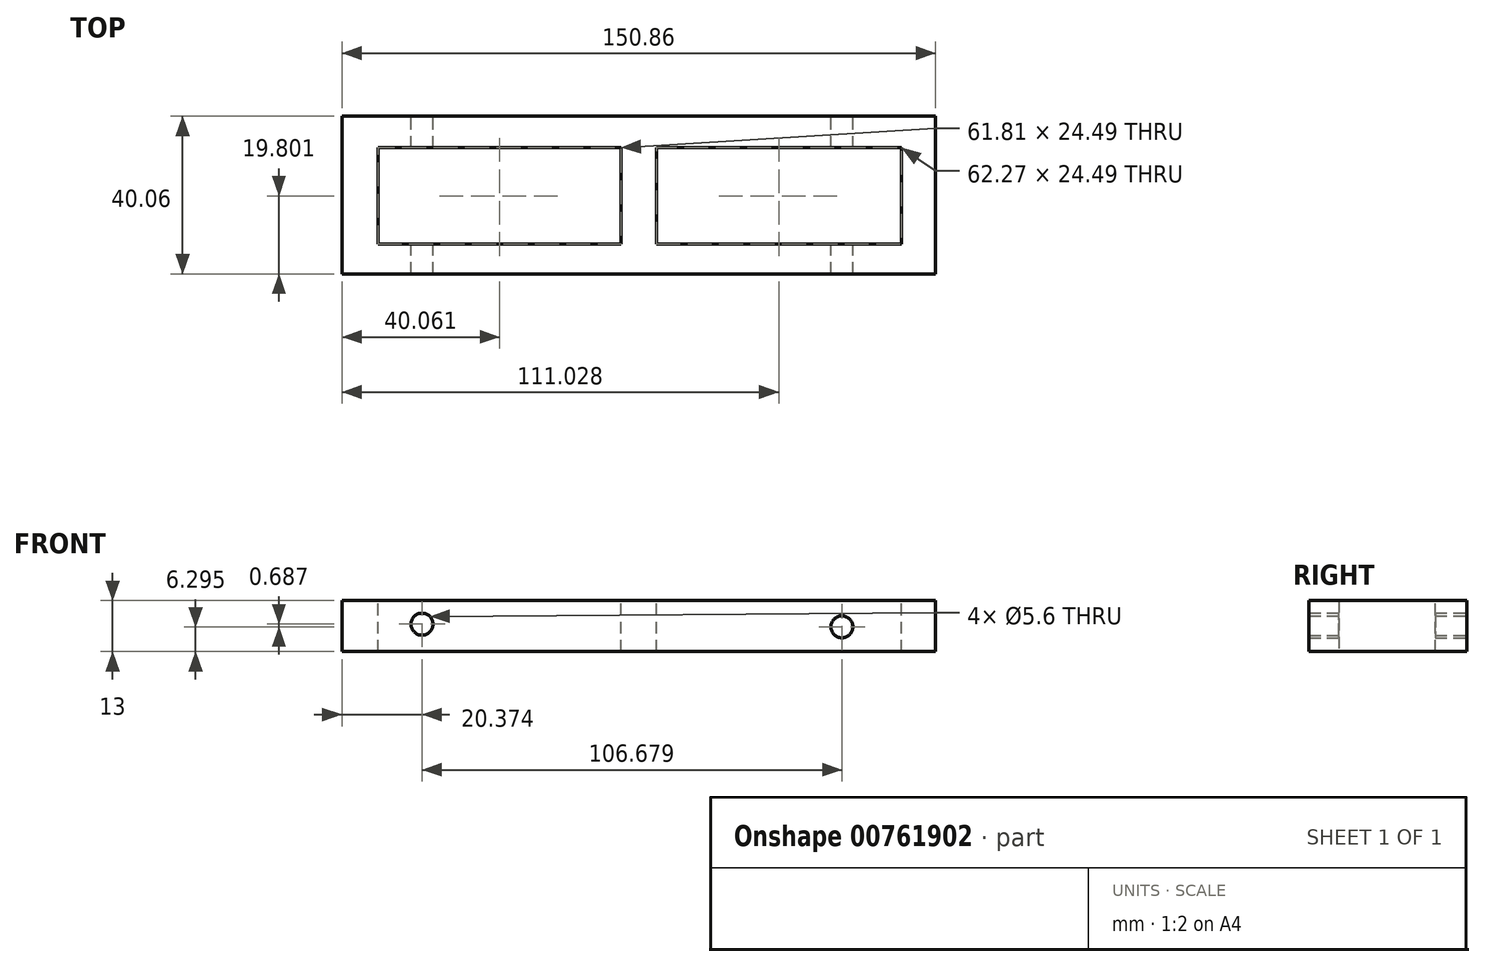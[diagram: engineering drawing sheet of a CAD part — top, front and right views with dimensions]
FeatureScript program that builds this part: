
annotation { "Feature Type Name" : "Feature", "Feature Type Description" : "" }
export const myFeature = defineFeature(function(context is Context, id is Id, definition is map)
    precondition{}
    {
        {
            var Q0;
            Q0=qCreatedBy(makeId("Top.planeOp"),FACE);
            var sketch = newSketch(context, id + "F0", { "sketchPlane" : qUnion([Q0])});
            skLineSegment(sketch, "E0.bottom", {"start": v(75.43, 20.03) * mm, "end": v(-75.43, 20.03) * mm});
            skLineSegment(sketch, "E0.top", {"start": v(75.43, -20.03) * mm, "end": v(-75.43, -20.03) * mm});
            skLineSegment(sketch, "E0.left", {"start": v(75.43, 20.03) * mm, "end": v(75.43, -20.03) * mm});
            skLineSegment(sketch, "E0.right", {"start": v(-75.43, 20.03) * mm, "end": v(-75.43, -20.03) * mm});
            skPoint(sketch, "E0.middle", {"position": v(0, 0) * mm});
            skSolve(sketch);
        }
        {
            var Q0;
            Q0=makeQuery(id+"F0.imprint","IMPRINT",FACE,{"disambiguationData":[TD([[makeQuery(id+"F0.imprint","IMPRINT",EDGE,{"derivedFrom":sQuery(id+"F0.wireOp",EDGE,"E0.bottom")}),1.0]])]});
            extrude(context, id + "F1", {"entities" : qUnion([Q0]), "depth" : 13 * mm, "offsetDistance" : 25 * mm});
        }
        {
            var Q0;
            Q0=makeQuery(id+"F1.opExtrude","CAP_FACE",FACE,{"disambiguationData":[OSD([sQuery(id+"F0.wireOp",EDGE,"E0.bottom"),sQuery(id+"F0.wireOp",EDGE,"E0.top"),sQuery(id+"F0.wireOp",EDGE,"E0.left"),sQuery(id+"F0.wireOp",EDGE,"E0.right")])],"isStart":false});
            var sketch = newSketch(context, id + "F2", { "sketchPlane" : qUnion([Q0])});
            skLineSegment(sketch, "E1", {"start": v(-66.27, 12.02) * mm, "end": v(-66.27, -12.48) * mm});
            skLineSegment(sketch, "E2", {"start": v(-66.27, -12.48) * mm, "end": v(66.73, -12.48) * mm});
            skLineSegment(sketch, "E3", {"start": v(66.73, -12.48) * mm, "end": v(66.73, 12.02) * mm});
            skLineSegment(sketch, "E4", {"start": v(66.73, 12.02) * mm, "end": v(-66.27, 12.02) * mm});
            skSolve(sketch);
        }
        {
            var Q0;
            Q0=makeQuery(id+"F2.imprint","IMPRINT",FACE,{"disambiguationData":[TD([[makeQuery(id+"F2.imprint","IMPRINT",EDGE,{"derivedFrom":sQuery(id+"F2.wireOp",EDGE,"E1")}),1.0]])]});
            extrude(context, id + "F3", {"entities" : qUnion([Q0]), "operationType" : NewBodyOperationType.REMOVE, "oppositeDirection" : true, "depth" : 25 * mm, "offsetDistance" : 25 * mm});
        }
        {
            var Q0;
            Q0=makeQuery(id+"F1.opExtrude","CAP_FACE",FACE,{"disambiguationData":[OSD([sQuery(id+"F0.wireOp",EDGE,"E0.bottom"),sQuery(id+"F0.wireOp",EDGE,"E0.top"),sQuery(id+"F0.wireOp",EDGE,"E0.left"),sQuery(id+"F0.wireOp",EDGE,"E0.right")])],"isStart":false});
            var sketch = newSketch(context, id + "F4", { "sketchPlane" : qUnion([Q0])});
            skLineSegment(sketch, "E5.bottom", {"start": v(-4.46, 16.37) * mm, "end": v(4.46, 16.37) * mm});
            skLineSegment(sketch, "E5.top", {"start": v(-4.46, -16.37) * mm, "end": v(4.46, -16.37) * mm});
            skLineSegment(sketch, "E5.left", {"start": v(-4.46, 16.37) * mm, "end": v(-4.46, -16.37) * mm});
            skLineSegment(sketch, "E5.right", {"start": v(4.46, 16.37) * mm, "end": v(4.46, -16.37) * mm});
            skPoint(sketch, "E5.middle", {"position": v(0, 0) * mm});
            skSolve(sketch);
        }
        {
            var Q0;
            Q0 = qSketchRegion(id + "F4", true);
            extrude(context, id + "F5", {"entities" : qUnion([Q0]), "operationType" : NewBodyOperationType.ADD, "oppositeDirection" : true, "depth" : 13 * mm, "offsetDistance" : 25 * mm});
        }
        {
            var Q0;
            Q0=makeQuery(id+"F1.opExtrude","SWEPT_FACE",FACE,{"disambiguationData":[OSD([sQuery(id+"F0.wireOp",EDGE,"E0.bottom")])]});
            var sketch = newSketch(context, id + "F6", { "sketchPlane" : qUnion([Q0])});
            skPoint(sketch, "E6", {"position": v(-51.62, 6.3) * mm});
            skPoint(sketch, "E7", {"position": v(55.06, 6.98) * mm});
            skSolve(sketch);
        }
        {
            var Q0;
            Q0=sQuery(id+"F6.wireOp",VERTEX,"E7");
            var Q1;
            Q1=sQuery(id+"F6.wireOp",VERTEX,"E6");
            var Q2;
            Q2=makeQuery(id+"F1.opExtrude","SWEPT_BODY",BODY,{"disambiguationData":[OSD([sQuery(id+"F0.wireOp",EDGE,"E0.bottom"),sQuery(id+"F0.wireOp",EDGE,"E0.top"),sQuery(id+"F0.wireOp",EDGE,"E0.left"),sQuery(id+"F0.wireOp",EDGE,"E0.right")])]});
            hole(context, id + "F7", {"style" : HoleStyle.SIMPLE, "endStyle" : HoleEndStyle.THROUGH, "holeDiameter" : 5.6 * mm, "majorDiameter" : 5 * mm, "isTappedThrough" : true, "tappedDepth" : 12 * mm, "tapClearance" : 3, "locations" : qUnion([Q0, Q1]), "scope" : qUnion([Q2])});
        }
    });
